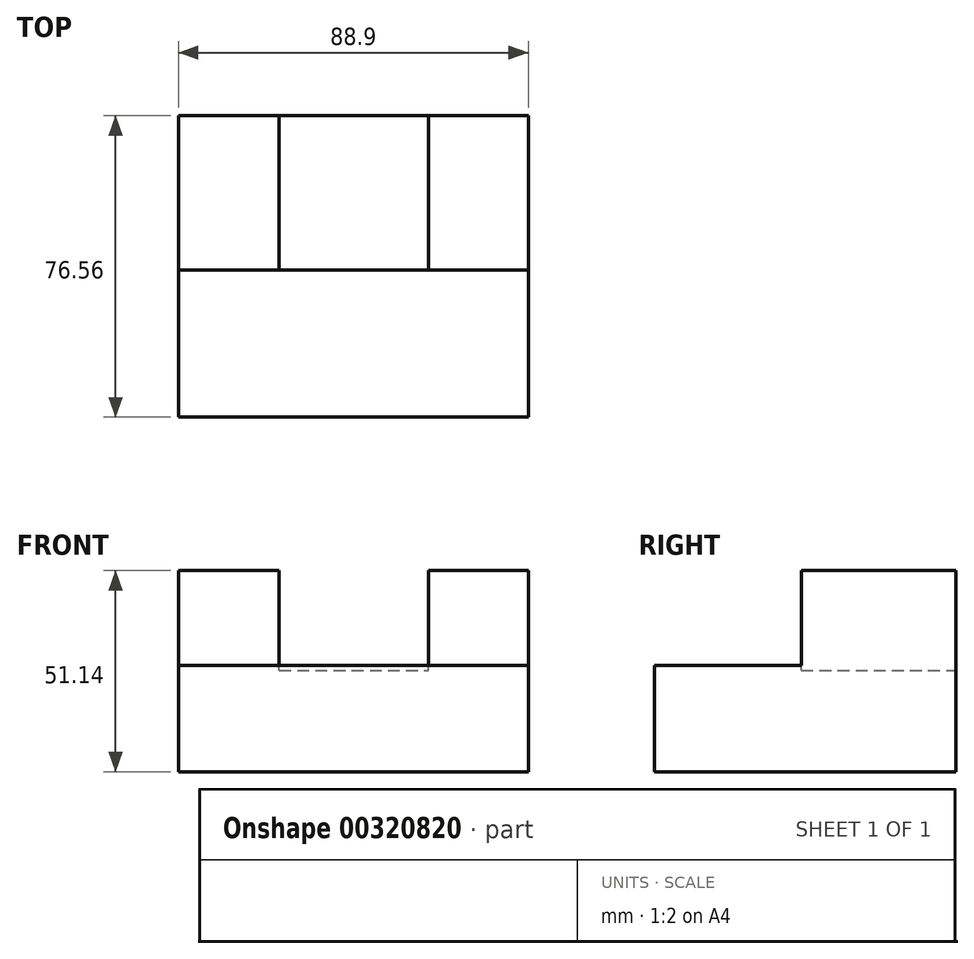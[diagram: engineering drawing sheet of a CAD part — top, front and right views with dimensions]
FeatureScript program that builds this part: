
annotation { "Feature Type Name" : "Feature", "Feature Type Description" : "" }
export const myFeature = defineFeature(function(context is Context, id is Id, definition is map)
    precondition{}
    {
        {
            var Q0;
            Q0=qCreatedBy(makeId("Right.planeOp"),FACE);
            var sketch = newSketch(context, id + "F0", { "sketchPlane" : qUnion([Q0])});
            skLineSegment(sketch, "E0", {"start": v(-23.69, 26.98) * mm, "end": v(15.53, 26.98) * mm});
            skLineSegment(sketch, "E1", {"start": v(15.53, 26.98) * mm, "end": v(15.53, -24.16) * mm});
            skLineSegment(sketch, "E2", {"start": v(15.53, -24.16) * mm, "end": v(-61.03, -24.16) * mm});
            skLineSegment(sketch, "E3", {"start": v(-61.03, -24.16) * mm, "end": v(-61.03, 2.82) * mm});
            skLineSegment(sketch, "E4", {"start": v(-61.03, 2.82) * mm, "end": v(-23.69, 2.82) * mm});
            skLineSegment(sketch, "E5", {"start": v(-23.69, 2.82) * mm, "end": v(-23.69, 26.98) * mm});
            skSolve(sketch);
        }
        {
            var Q0;
            Q0=makeQuery(id+"F0.imprint","IMPRINT",FACE,{"disambiguationData":[TD([[makeQuery(id+"F0.imprint","IMPRINT",EDGE,{"derivedFrom":sQuery(id+"F0.wireOp",EDGE,"E0")}),-1.0]])]});
            extrude(context, id + "F1", {"entities" : qUnion([Q0]), "oppositeDirection" : true, "depth" : 88.9 * mm});
        }
        {
            var Q0;
            Q0=makeQuery(id+"F1.opExtrude","SWEPT_FACE",FACE,{"disambiguationData":[OSD([sQuery(id+"F0.wireOp",EDGE,"E0")])]});
            var sketch = newSketch(context, id + "F2", { "sketchPlane" : qUnion([Q0])});
            skLineSegment(sketch, "E6", {"start": v(-63.3, -4.08) * mm, "end": v(-63.3, 15.53) * mm});
            skLineSegment(sketch, "E7", {"start": v(-63.3, 15.53) * mm, "end": v(-25.33, 15.53) * mm});
            skLineSegment(sketch, "E8", {"start": v(-25.33, 15.53) * mm, "end": v(-25.33, -4.08) * mm});
            skLineSegment(sketch, "E9", {"start": v(-63.3, -4.08) * mm, "end": v(-63.3, -23.69) * mm});
            skLineSegment(sketch, "E10", {"start": v(-63.3, -23.69) * mm, "end": v(-25.33, -23.69) * mm});
            skLineSegment(sketch, "E11", {"start": v(-25.33, -23.69) * mm, "end": v(-25.33, -4.08) * mm});
            skSolve(sketch);
        }
        {
            var Q0;
            Q0=makeQuery(id+"F2.imprint","IMPRINT",FACE,{"disambiguationData":[TD([[makeQuery(id+"F2.imprint","IMPRINT",EDGE,{"derivedFrom":sQuery(id+"F2.wireOp",EDGE,"E6")}),-1.0]])]});
            extrude(context, id + "F3", {"entities" : qUnion([Q0]), "operationType" : NewBodyOperationType.REMOVE, "oppositeDirection" : true, "depth" : 25.4 * mm});
        }
    });
